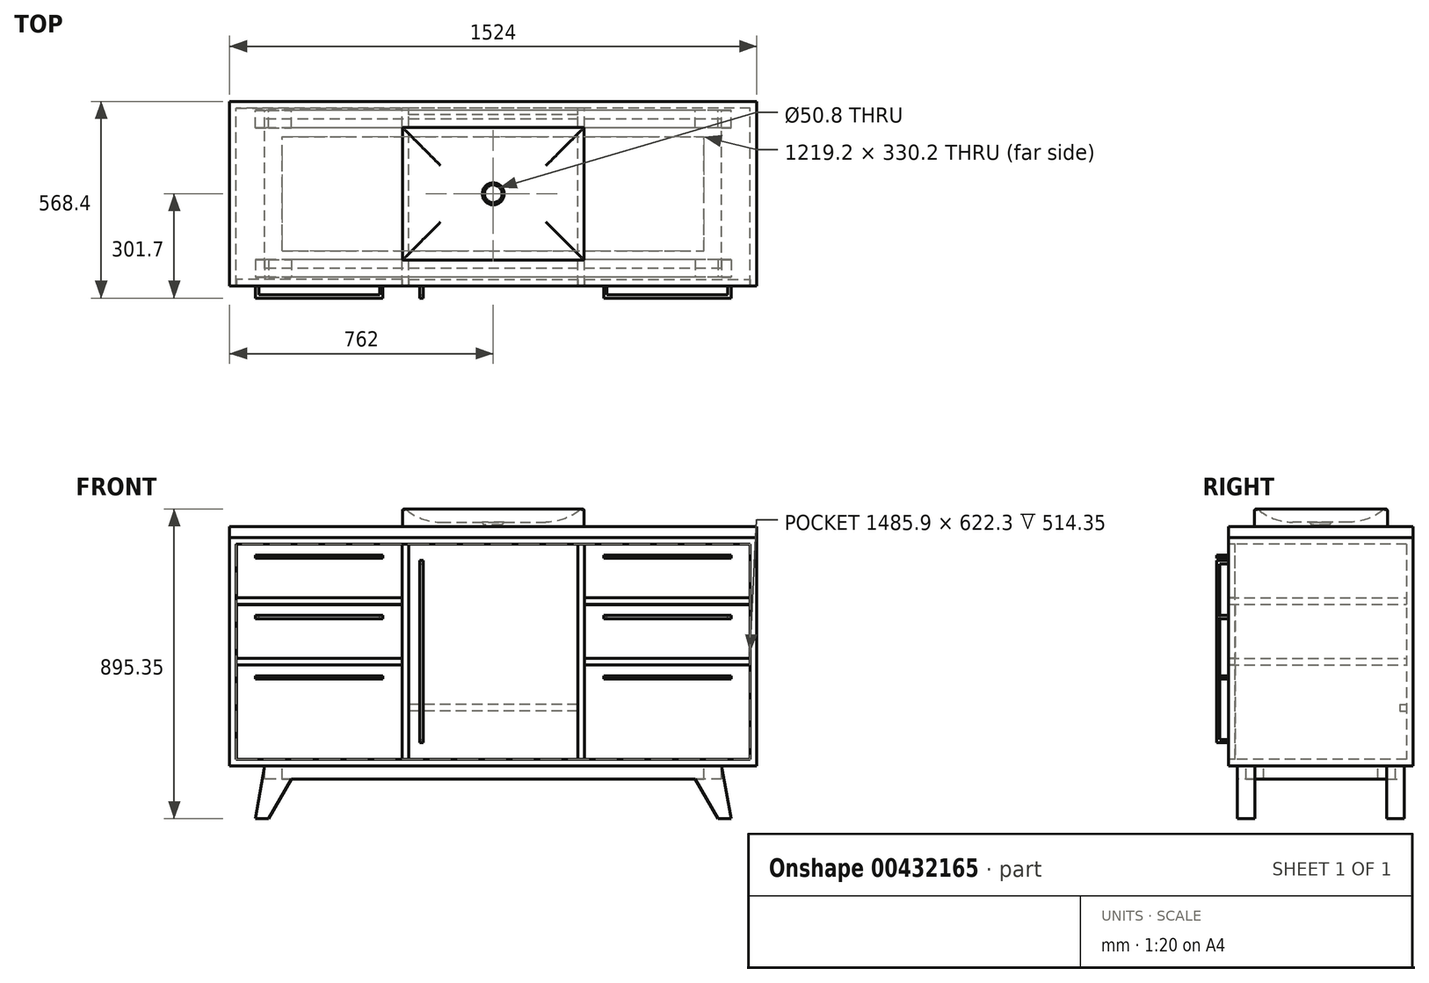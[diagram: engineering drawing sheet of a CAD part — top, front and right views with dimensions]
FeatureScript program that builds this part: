
annotation { "Feature Type Name" : "Feature", "Feature Type Description" : "" }
export const myFeature = defineFeature(function(context is Context, id is Id, definition is map)
    precondition{}
    {
        {
            var Q0;
            Q0=qCreatedBy(makeId("Front.planeOp"),FACE);
            var sketch = newSketch(context, id + "F0", { "sketchPlane" : qUnion([Q0])});
            skLineSegment(sketch, "E0.bottom", {"start": v(762, 330.2) * mm, "end": v(-762, 330.2) * mm});
            skLineSegment(sketch, "E0.top", {"start": v(762, -330.2) * mm, "end": v(-762, -330.2) * mm});
            skLineSegment(sketch, "E0.left", {"start": v(762, 330.2) * mm, "end": v(762, -330.2) * mm});
            skLineSegment(sketch, "E0.right", {"start": v(-762, 330.2) * mm, "end": v(-762, -330.2) * mm});
            skPoint(sketch, "E0.middle", {"position": v(0, 0) * mm});
            skSolve(sketch);
        }
        {
            var Q0;
            Q0=makeQuery(id+"F0.imprint","IMPRINT",FACE,{"disambiguationData":[TD([[makeQuery(id+"F0.imprint","IMPRINT",EDGE,{"derivedFrom":sQuery(id+"F0.wireOp",EDGE,"E0.bottom")}),1.0]])]});
            extrude(context, id + "F1", {"entities" : qUnion([Q0]), "oppositeDirection" : true, "depth" : 533.4 * mm});
        }
        {
            var Q0;
            Q0=makeQuery(id+"F1.opExtrude","CAP_FACE",FACE,{"disambiguationData":[OSD([sQuery(id+"F0.wireOp",EDGE,"E0.bottom"),sQuery(id+"F0.wireOp",EDGE,"E0.top"),sQuery(id+"F0.wireOp",EDGE,"E0.left"),sQuery(id+"F0.wireOp",EDGE,"E0.right")])],"isStart":true});
            var sketch = newSketch(context, id + "F2", { "sketchPlane" : qUnion([Q0])});
            skLineSegment(sketch, "E1.bottom", {"start": v(742.95, 311.15) * mm, "end": v(-742.95, 311.15) * mm});
            skLineSegment(sketch, "E1.top", {"start": v(742.95, -311.15) * mm, "end": v(-742.95, -311.15) * mm});
            skLineSegment(sketch, "E1.left", {"start": v(742.95, 311.15) * mm, "end": v(742.95, -311.15) * mm});
            skLineSegment(sketch, "E1.right", {"start": v(-742.95, 311.15) * mm, "end": v(-742.95, -311.15) * mm});
            skPoint(sketch, "E1.middle", {"position": v(0, 0) * mm});
            skSolve(sketch);
        }
        {
            var Q0;
            Q0=makeQuery(id+"F2.imprint","IMPRINT",FACE,{"disambiguationData":[TD([[makeQuery(id+"F2.imprint","IMPRINT",EDGE,{"derivedFrom":sQuery(id+"F2.wireOp",EDGE,"E1.bottom")}),1.0]])]});
            extrude(context, id + "F3", {"entities" : qUnion([Q0]), "operationType" : NewBodyOperationType.REMOVE, "oppositeDirection" : true, "depth" : 514.35 * mm});
        }
        {
            var Q0;
            Q0=makeQuery(id+"F3.boolean.opBoolean","COPY",FACE,{"derivedFrom":makeQuery(id+"F3.opExtrude","CAP_FACE",FACE,{"disambiguationData":[OSD([sQuery(id+"F2.wireOp",EDGE,"E1.bottom"),sQuery(id+"F2.wireOp",EDGE,"E1.top"),sQuery(id+"F2.wireOp",EDGE,"E1.left"),sQuery(id+"F2.wireOp",EDGE,"E1.right")])],"isStart":false})});
            var sketch = newSketch(context, id + "F4", { "sketchPlane" : qUnion([Q0])});
            skLineSegment(sketch, "E2.bottom", {"start": v(-263.52, 311.15) * mm, "end": v(-244.47, 311.15) * mm});
            skLineSegment(sketch, "E2.top", {"start": v(-263.52, -311.15) * mm, "end": v(-244.47, -311.15) * mm});
            skLineSegment(sketch, "E2.left", {"start": v(-263.53, 311.15) * mm, "end": v(-263.53, -311.15) * mm});
            skLineSegment(sketch, "E2.right", {"start": v(-244.47, 311.15) * mm, "end": v(-244.47, -311.15) * mm});
            skPoint(sketch, "E2.middle", {"position": v(-254, 0) * mm});
            skLineSegment(sketch, "E3.bottom", {"start": v(244.47, 311.15) * mm, "end": v(263.52, 311.15) * mm});
            skLineSegment(sketch, "E3.top", {"start": v(244.47, -311.15) * mm, "end": v(263.52, -311.15) * mm});
            skLineSegment(sketch, "E3.left", {"start": v(244.47, 311.15) * mm, "end": v(244.47, -311.15) * mm});
            skLineSegment(sketch, "E3.right", {"start": v(263.53, 311.15) * mm, "end": v(263.53, -311.15) * mm});
            skPoint(sketch, "E3.middle", {"position": v(254, 0) * mm});
            skLineSegment(sketch, "E4", {"start": v(-742.95, 0) * mm, "end": v(742.95, 0) * mm, "construction": true});
            skSolve(sketch);
        }
        {
            var Q0;
            Q0=makeQuery(id+"F4.imprint","IMPRINT",FACE,{"disambiguationData":[TD([[makeQuery(id+"F4.imprint","IMPRINT",EDGE,{"derivedFrom":sQuery(id+"F4.wireOp",EDGE,"E2.bottom")}),1.0]])]});
            var Q1;
            Q1=makeQuery(id+"F4.imprint","IMPRINT",FACE,{"disambiguationData":[TD([[makeQuery(id+"F4.imprint","IMPRINT",EDGE,{"derivedFrom":sQuery(id+"F4.wireOp",EDGE,"E3.bottom")}),1.0]])]});
            var Q2;
            Q2=makeQuery(id+"F1.opExtrude","CAP_FACE",FACE,{"disambiguationData":[OSD([sQuery(id+"F0.wireOp",EDGE,"E0.bottom"),sQuery(id+"F0.wireOp",EDGE,"E0.top"),sQuery(id+"F0.wireOp",EDGE,"E0.left"),sQuery(id+"F0.wireOp",EDGE,"E0.right")])],"isStart":true});
            extrude(context, id + "F5", {"entities" : qUnion([Q0, Q1]), "endBound" : BoundingType.UP_TO_SURFACE, "endBoundEntityFace" : qUnion([Q2]), "depth" : ((2 * 12) - .75 - .75) * mm});
        }
        {
            var Q0;
            Q0=makeQuery(id+"F3.boolean.opBoolean","COPY",FACE,{"derivedFrom":makeQuery(id+"F3.opExtrude","CAP_FACE",FACE,{"disambiguationData":[OSD([sQuery(id+"F2.wireOp",EDGE,"E1.bottom"),sQuery(id+"F2.wireOp",EDGE,"E1.top"),sQuery(id+"F2.wireOp",EDGE,"E1.left"),sQuery(id+"F2.wireOp",EDGE,"E1.right")])],"isStart":false})});
            var sketch = newSketch(context, id + "F6", { "sketchPlane" : qUnion([Q0])});
            skLineSegment(sketch, "E5", {"start": v(-742.95, 311.15) * mm, "end": v(-263.53, 311.15) * mm, "construction": true});
            skLineSegment(sketch, "E6.bottom", {"start": v(-742.95, 155.58) * mm, "end": v(-263.53, 155.58) * mm});
            skLineSegment(sketch, "E6.top", {"start": v(-742.95, 136.53) * mm, "end": v(-263.53, 136.53) * mm});
            skLineSegment(sketch, "E6.left", {"start": v(-742.95, 155.58) * mm, "end": v(-742.95, 136.53) * mm});
            skLineSegment(sketch, "E6.right", {"start": v(-263.53, 155.58) * mm, "end": v(-263.53, 136.53) * mm});
            skPoint(sketch, "E6.middle", {"position": v(-503.24, 146.05) * mm});
            skPoint(sketch, "E6.middle.positionSnap0", {"position": v(-503.24, 311.15) * mm});
            skPoint(sketch, "E6.centerSnap0", {"position": v(-503.24, 311.15) * mm});
            skLineSegment(sketch, "E7.bottom", {"start": v(-742.95, -19.05) * mm, "end": v(-263.53, -19.05) * mm});
            skLineSegment(sketch, "E7.top", {"start": v(-742.95, -38.1) * mm, "end": v(-263.53, -38.1) * mm});
            skLineSegment(sketch, "E7.left", {"start": v(-742.95, -19.05) * mm, "end": v(-742.95, -38.1) * mm});
            skLineSegment(sketch, "E7.right", {"start": v(-263.53, -19.05) * mm, "end": v(-263.53, -38.1) * mm});
            skPoint(sketch, "E7.middle", {"position": v(-503.24, -28.57) * mm});
            skLineSegment(sketch, "E8", {"start": v(0, 311.15) * mm, "end": v(0, -311.15) * mm, "construction": true});
            skLineSegment(sketch, "E9.MirrorCS", {"start": v(263.53, -19.05) * mm, "end": v(263.53, -38.1) * mm});
            skLineSegment(sketch, "E10.MirrorCS", {"start": v(742.95, -19.05) * mm, "end": v(742.95, -38.1) * mm});
            skLineSegment(sketch, "E11.MirrorCS", {"start": v(742.95, 155.58) * mm, "end": v(742.95, 136.53) * mm});
            skLineSegment(sketch, "E12.MirrorCS", {"start": v(263.53, 155.58) * mm, "end": v(263.53, 136.53) * mm});
            skPoint(sketch, "E13.MirrorP", {"position": v(503.24, 311.15) * mm});
            skLineSegment(sketch, "E14.MirrorCS", {"start": v(742.95, 155.58) * mm, "end": v(263.53, 155.57) * mm});
            skPoint(sketch, "E15.MirrorP", {"position": v(503.24, -28.57) * mm});
            skLineSegment(sketch, "E16.MirrorCS", {"start": v(742.95, -38.1) * mm, "end": v(263.53, -38.1) * mm});
            skLineSegment(sketch, "E17.MirrorCS", {"start": v(742.95, -19.05) * mm, "end": v(263.53, -19.05) * mm});
            skLineSegment(sketch, "E18.MirrorCS", {"start": v(742.95, 136.53) * mm, "end": v(263.53, 136.53) * mm});
            skLineSegment(sketch, "E19.MirrorCS", {"start": v(742.95, 311.15) * mm, "end": v(263.53, 311.15) * mm, "construction": true});
            skPoint(sketch, "E20.MirrorP", {"position": v(503.24, 146.05) * mm});
            skPoint(sketch, "E21.cornerSnap0", {"position": v(-503.24, -19.05) * mm});
            skPoint(sketch, "E22.middle", {"position": v(0, 146.05) * mm});
            skLineSegment(sketch, "E23.bottom", {"start": v(244.47, -152.4) * mm, "end": v(-244.47, -152.4) * mm});
            skLineSegment(sketch, "E23.top", {"start": v(244.47, -171.45) * mm, "end": v(-244.47, -171.45) * mm});
            skLineSegment(sketch, "E23.left", {"start": v(244.47, -152.4) * mm, "end": v(244.47, -171.45) * mm});
            skLineSegment(sketch, "E23.right", {"start": v(-244.47, -152.4) * mm, "end": v(-244.47, -171.45) * mm});
            skPoint(sketch, "E23.middle", {"position": v(0, -161.93) * mm});
            skSolve(sketch);
        }
        {
            var Q0;
            Q0=makeQuery(id+"F6.imprint","IMPRINT",FACE,{"disambiguationData":[TD([[makeQuery(id+"F6.imprint","IMPRINT",EDGE,{"derivedFrom":sQuery(id+"F6.wireOp",EDGE,"E6.bottom")}),-1.0]])]});
            var Q1;
            Q1=makeQuery(id+"F6.imprint","IMPRINT",FACE,{"disambiguationData":[TD([[makeQuery(id+"F6.imprint","IMPRINT",EDGE,{"derivedFrom":sQuery(id+"F6.wireOp",EDGE,"E7.bottom")}),-1.0]])]});
            var Q2;
            Q2=makeQuery(id+"F6.imprint","IMPRINT",FACE,{"disambiguationData":[TD([[makeQuery(id+"F6.imprint","IMPRINT",EDGE,{"derivedFrom":sQuery(id+"F6.wireOp",EDGE,"E11.MirrorCS")}),-1.0]])]});
            var Q3;
            Q3=makeQuery(id+"F6.imprint","IMPRINT",FACE,{"disambiguationData":[TD([[makeQuery(id+"F6.imprint","IMPRINT",EDGE,{"derivedFrom":sQuery(id+"F6.wireOp",EDGE,"E9.MirrorCS")}),1.0]])]});
            var Q4;
            Q4=makeQuery(id+"F1.opExtrude","CAP_FACE",FACE,{"disambiguationData":[OSD([sQuery(id+"F0.wireOp",EDGE,"E0.bottom"),sQuery(id+"F0.wireOp",EDGE,"E0.top"),sQuery(id+"F0.wireOp",EDGE,"E0.left"),sQuery(id+"F0.wireOp",EDGE,"E0.right")])],"isStart":true});
            extrude(context, id + "F7", {"entities" : qUnion([Q0, Q1, Q2, Q3]), "endBound" : BoundingType.UP_TO_SURFACE, "endBoundEntityFace" : qUnion([Q4]), "depth" : 571.5 * mm});
        }
        {
            var Q0;
            Q0=makeQuery(id+"F7.opExtrude","CAP_FACE",FACE,{"disambiguationData":[OSD([sQuery(id+"F6.wireOp",EDGE,"E7.bottom"),sQuery(id+"F6.wireOp",EDGE,"E7.top"),sQuery(id+"F6.wireOp",EDGE,"E7.left"),sQuery(id+"F6.wireOp",EDGE,"E7.right")])],"isStart":false});
            var sketch = newSketch(context, id + "F8", { "sketchPlane" : qUnion([Q0])});
            skLineSegment(sketch, "E24.bottom", {"start": v(-742.95, -38.1) * mm, "end": v(-263.53, -38.1) * mm, "construction": true});
            skLineSegment(sketch, "E24.top", {"start": v(-742.95, -311.15) * mm, "end": v(-263.53, -311.15) * mm, "construction": true});
            skLineSegment(sketch, "E24.left", {"start": v(-742.95, -38.1) * mm, "end": v(-742.95, -311.15) * mm, "construction": true});
            skLineSegment(sketch, "E24.right", {"start": v(-263.52, -38.1) * mm, "end": v(-263.52, -311.15) * mm, "construction": true});
            skLineSegment(sketch, "E25.bottom", {"start": v(-742.95, -19.05) * mm, "end": v(-263.53, -19.05) * mm, "construction": true});
            skLineSegment(sketch, "E25.top", {"start": v(-742.95, 136.53) * mm, "end": v(-263.53, 136.53) * mm, "construction": true});
            skLineSegment(sketch, "E25.left", {"start": v(-742.95, -19.05) * mm, "end": v(-742.95, 136.53) * mm, "construction": true});
            skLineSegment(sketch, "E25.right", {"start": v(-263.53, -19.05) * mm, "end": v(-263.53, 136.53) * mm, "construction": true});
            skLineSegment(sketch, "E26.bottom", {"start": v(-742.95, 311.15) * mm, "end": v(-263.53, 311.15) * mm, "construction": true});
            skLineSegment(sketch, "E26.top", {"start": v(-742.95, 155.58) * mm, "end": v(-263.53, 155.58) * mm, "construction": true});
            skLineSegment(sketch, "E26.left", {"start": v(-742.95, 311.15) * mm, "end": v(-742.95, 155.58) * mm, "construction": true});
            skLineSegment(sketch, "E26.right", {"start": v(-263.52, 311.15) * mm, "end": v(-263.52, 155.58) * mm, "construction": true});
            skLineSegment(sketch, "E27", {"start": v(0, 311.15) * mm, "end": v(0, -311.15) * mm, "construction": true});
            skLineSegment(sketch, "E28.bottom", {"start": v(-263.92, 155.97) * mm, "end": v(-742.55, 155.97) * mm});
            skLineSegment(sketch, "E28.top", {"start": v(-263.92, 310.75) * mm, "end": v(-742.55, 310.75) * mm});
            skLineSegment(sketch, "E28.left", {"start": v(-263.92, 155.97) * mm, "end": v(-263.92, 310.75) * mm});
            skLineSegment(sketch, "E28.right", {"start": v(-742.55, 155.97) * mm, "end": v(-742.55, 310.75) * mm});
            skPoint(sketch, "E28.middle", {"position": v(-503.24, 233.36) * mm});
            skPoint(sketch, "E28.middle.positionSnap0", {"position": v(-503.24, 311.15) * mm});
            skPoint(sketch, "E28.middle.positionSnap1", {"position": v(-742.95, 233.36) * mm});
            skPoint(sketch, "E28.centerSnap0", {"position": v(-503.24, 311.15) * mm});
            skPoint(sketch, "E28.centerSnap1", {"position": v(-742.95, 233.36) * mm});
            skPoint(sketch, "E29.middle.positionSnap0", {"position": v(-503.24, 136.53) * mm});
            skPoint(sketch, "E29.middle.positionSnap1", {"position": v(-742.95, 58.74) * mm});
            skPoint(sketch, "E29.centerSnap0", {"position": v(-503.24, 136.53) * mm});
            skPoint(sketch, "E29.centerSnap1", {"position": v(-742.95, 58.74) * mm});
            skLineSegment(sketch, "E30.bottom", {"start": v(-263.92, -38.5) * mm, "end": v(-742.55, -38.5) * mm});
            skLineSegment(sketch, "E30.top", {"start": v(-263.92, -310.75) * mm, "end": v(-742.55, -310.75) * mm});
            skLineSegment(sketch, "E30.left", {"start": v(-263.92, -38.5) * mm, "end": v(-263.92, -310.75) * mm});
            skLineSegment(sketch, "E30.right", {"start": v(-742.55, -38.5) * mm, "end": v(-742.55, -310.75) * mm});
            skPoint(sketch, "E30.middle", {"position": v(-503.24, -174.63) * mm});
            skPoint(sketch, "E30.middle.positionSnap0", {"position": v(-742.95, -174.63) * mm});
            skPoint(sketch, "E30.middle.positionSnap1", {"position": v(-503.24, -38.1) * mm});
            skPoint(sketch, "E30.centerSnap0", {"position": v(-742.95, -174.63) * mm});
            skPoint(sketch, "E30.centerSnap1", {"position": v(-503.24, -38.1) * mm});
            skLineSegment(sketch, "E31.bottom", {"start": v(-742.55, 136.13) * mm, "end": v(-263.92, 136.13) * mm});
            skLineSegment(sketch, "E31.top", {"start": v(-742.55, -18.65) * mm, "end": v(-263.92, -18.65) * mm});
            skLineSegment(sketch, "E31.left", {"start": v(-742.55, 136.13) * mm, "end": v(-742.55, -18.65) * mm});
            skLineSegment(sketch, "E31.right", {"start": v(-263.92, 136.13) * mm, "end": v(-263.92, -18.65) * mm});
            skPoint(sketch, "E31.middle", {"position": v(-503.24, 58.74) * mm});
            skLineSegment(sketch, "E32.MirrorCS", {"start": v(742.55, 155.97) * mm, "end": v(742.55, 310.75) * mm});
            skLineSegment(sketch, "E33.MirrorCS", {"start": v(742.55, 136.13) * mm, "end": v(742.55, -18.65) * mm});
            skLineSegment(sketch, "E34.MirrorCS", {"start": v(263.92, -310.75) * mm, "end": v(742.55, -310.75) * mm});
            skPoint(sketch, "E35.MirrorP", {"position": v(742.95, -174.62) * mm});
            skLineSegment(sketch, "E36.MirrorCS", {"start": v(742.55, -18.65) * mm, "end": v(263.92, -18.65) * mm});
            skLineSegment(sketch, "E37.MirrorCS", {"start": v(263.92, 155.97) * mm, "end": v(742.55, 155.97) * mm});
            skLineSegment(sketch, "E38.MirrorCS", {"start": v(263.92, -38.5) * mm, "end": v(263.92, -310.75) * mm});
            skPoint(sketch, "E39.MirrorP", {"position": v(503.24, 311.15) * mm});
            skPoint(sketch, "E40.MirrorP", {"position": v(503.24, -38.1) * mm});
            skLineSegment(sketch, "E41.MirrorCS", {"start": v(263.92, 310.75) * mm, "end": v(742.55, 310.75) * mm});
            skLineSegment(sketch, "E42.MirrorCS", {"start": v(742.55, 136.13) * mm, "end": v(263.92, 136.13) * mm});
            skPoint(sketch, "E43.MirrorP", {"position": v(742.95, 233.36) * mm});
            skLineSegment(sketch, "E44.MirrorCS", {"start": v(263.92, 155.97) * mm, "end": v(263.92, 310.75) * mm});
            skLineSegment(sketch, "E45.MirrorCS", {"start": v(742.55, -38.5) * mm, "end": v(742.55, -310.75) * mm});
            skPoint(sketch, "E46.MirrorP", {"position": v(503.24, 136.53) * mm});
            skLineSegment(sketch, "E47.MirrorCS", {"start": v(263.92, 136.13) * mm, "end": v(263.92, -18.65) * mm});
            skPoint(sketch, "E48.MirrorP", {"position": v(742.95, 58.74) * mm});
            skPoint(sketch, "E49.MirrorP", {"position": v(503.24, 233.36) * mm});
            skLineSegment(sketch, "E50.MirrorCS", {"start": v(742.95, -311.15) * mm, "end": v(263.53, -311.15) * mm, "construction": true});
            skLineSegment(sketch, "E51.MirrorCS", {"start": v(742.95, -19.05) * mm, "end": v(742.95, 136.53) * mm, "construction": true});
            skLineSegment(sketch, "E52.MirrorCS", {"start": v(742.95, -38.1) * mm, "end": v(742.95, -311.15) * mm, "construction": true});
            skPoint(sketch, "E53.MirrorP", {"position": v(503.24, 58.74) * mm});
            skLineSegment(sketch, "E54.MirrorCS", {"start": v(263.52, -38.1) * mm, "end": v(263.52, -311.15) * mm, "construction": true});
            skLineSegment(sketch, "E55.MirrorCS", {"start": v(742.95, -19.05) * mm, "end": v(263.53, -19.05) * mm, "construction": true});
            skLineSegment(sketch, "E56.MirrorCS", {"start": v(263.52, 311.15) * mm, "end": v(263.52, 155.58) * mm, "construction": true});
            skLineSegment(sketch, "E57.MirrorCS", {"start": v(742.95, 311.15) * mm, "end": v(742.95, 155.58) * mm, "construction": true});
            skLineSegment(sketch, "E58.MirrorCS", {"start": v(742.95, -38.1) * mm, "end": v(263.53, -38.1) * mm, "construction": true});
            skLineSegment(sketch, "E59.MirrorCS", {"start": v(742.95, 155.58) * mm, "end": v(263.53, 155.58) * mm, "construction": true});
            skLineSegment(sketch, "E60.MirrorCS", {"start": v(742.95, 136.53) * mm, "end": v(263.53, 136.53) * mm, "construction": true});
            skPoint(sketch, "E61.MirrorP", {"position": v(503.24, -174.62) * mm});
            skLineSegment(sketch, "E62.MirrorCS", {"start": v(263.53, -19.05) * mm, "end": v(263.53, 136.53) * mm, "construction": true});
            skLineSegment(sketch, "E63.MirrorCS", {"start": v(263.92, -38.5) * mm, "end": v(742.55, -38.5) * mm});
            skLineSegment(sketch, "E64.MirrorCS", {"start": v(742.95, 311.15) * mm, "end": v(263.53, 311.15) * mm, "construction": true});
            skSolve(sketch);
        }
        {
            var Q0;
            Q0=makeQuery(id+"F8.imprint","IMPRINT",FACE,{"disambiguationData":[TD([[makeQuery(id+"F8.imprint","IMPRINT",EDGE,{"derivedFrom":sQuery(id+"F8.wireOp",EDGE,"E28.bottom")}),-1.0]])]});
            var Q1;
            Q1=makeQuery(id+"F8.imprint","IMPRINT",FACE,{"disambiguationData":[TD([[makeQuery(id+"F8.imprint","IMPRINT",EDGE,{"derivedFrom":sQuery(id+"F8.wireOp",EDGE,"E31.bottom")}),-1.0]])]});
            var Q2;
            Q2=makeQuery(id+"F8.imprint","IMPRINT",FACE,{"disambiguationData":[TD([[makeQuery(id+"F8.imprint","IMPRINT",EDGE,{"derivedFrom":sQuery(id+"F8.wireOp",EDGE,"E30.bottom")}),1.0]])]});
            var Q3;
            Q3=makeQuery(id+"F8.imprint","IMPRINT",FACE,{"disambiguationData":[TD([[makeQuery(id+"F8.imprint","IMPRINT",EDGE,{"derivedFrom":sQuery(id+"F8.wireOp",EDGE,"E32.MirrorCS")}),1.0]])]});
            var Q4;
            Q4=makeQuery(id+"F8.imprint","IMPRINT",FACE,{"disambiguationData":[TD([[makeQuery(id+"F8.imprint","IMPRINT",EDGE,{"derivedFrom":sQuery(id+"F8.wireOp",EDGE,"E33.MirrorCS")}),-1.0]])]});
            var Q5;
            Q5=makeQuery(id+"F8.imprint","IMPRINT",FACE,{"disambiguationData":[TD([[makeQuery(id+"F8.imprint","IMPRINT",EDGE,{"derivedFrom":sQuery(id+"F8.wireOp",EDGE,"E34.MirrorCS")}),1.0]])]});
            extrude(context, id + "F9", {"entities" : qUnion([Q0, Q1, Q2, Q3, Q4, Q5]), "oppositeDirection" : true, "depth" : 19.05 * mm});
        }
        {
            var Q0;
            Q0=qCreatedBy(makeId("Front.planeOp"),FACE);
            var sketch = newSketch(context, id + "F10", { "sketchPlane" : qUnion([Q0])});
            skLineSegment(sketch, "E65.bottom", {"start": v(-244.08, -310.75) * mm, "end": v(244.08, -310.75) * mm});
            skLineSegment(sketch, "E65.top", {"start": v(-244.08, 310.75) * mm, "end": v(244.08, 310.75) * mm});
            skLineSegment(sketch, "E65.left", {"start": v(-244.08, -310.75) * mm, "end": v(-244.08, 310.75) * mm});
            skLineSegment(sketch, "E65.right", {"start": v(244.08, -310.75) * mm, "end": v(244.08, 310.75) * mm});
            skPoint(sketch, "E65.middle", {"position": v(0, 0) * mm});
            skSolve(sketch);
        }
        {
            var Q0;
            Q0=makeQuery(id+"F10.imprint","IMPRINT",FACE,{"disambiguationData":[TD([[makeQuery(id+"F10.imprint","IMPRINT",EDGE,{"derivedFrom":sQuery(id+"F10.wireOp",EDGE,"E65.bottom")}),1.0]])]});
            extrude(context, id + "F11", {"entities" : qUnion([Q0]), "oppositeDirection" : true, "depth" : 19.05 * mm});
        }
        {
            var Q0;
            Q0=makeQuery(id+"F6.imprint","IMPRINT",FACE,{"disambiguationData":[TD([[makeQuery(id+"F6.imprint","IMPRINT",EDGE,{"derivedFrom":sQuery(id+"F6.wireOp",EDGE,"E23.bottom")}),1.0]])]});
            extrude(context, id + "F12", {"entities" : qUnion([Q0]), "depth" : ((21 - .75 - .75) - .3125) * mm});
        }
        {
            var Q0;
            Q0=makeQuery(id+"F1.opExtrude","SWEPT_FACE",FACE,{"disambiguationData":[OSD([sQuery(id+"F0.wireOp",EDGE,"E0.top")])]});
            var sketch = newSketch(context, id + "F13", { "sketchPlane" : qUnion([Q0])});
            skLineSegment(sketch, "E66.bottom", {"start": v(660.4, -50.8) * mm, "end": v(-660.4, -50.8) * mm});
            skLineSegment(sketch, "E66.top", {"start": v(660.4, -482.6) * mm, "end": v(-660.4, -482.6) * mm});
            skLineSegment(sketch, "E66.left", {"start": v(660.4, -50.8) * mm, "end": v(660.4, -482.6) * mm});
            skLineSegment(sketch, "E66.right", {"start": v(-660.4, -50.8) * mm, "end": v(-660.4, -482.6) * mm});
            skPoint(sketch, "E66.middle", {"position": v(0, -266.7) * mm});
            skPoint(sketch, "E66.middle.positionSnap0", {"position": v(-762, -266.7) * mm});
            skPoint(sketch, "E66.centerSnap0", {"position": v(-762, -266.7) * mm});
            skLineSegment(sketch, "E67.bottom", {"start": v(-609.6, -101.6) * mm, "end": v(609.6, -101.6) * mm});
            skLineSegment(sketch, "E67.top", {"start": v(-609.6, -431.8) * mm, "end": v(609.6, -431.8) * mm});
            skLineSegment(sketch, "E67.left", {"start": v(-609.6, -101.6) * mm, "end": v(-609.6, -431.8) * mm});
            skLineSegment(sketch, "E67.right", {"start": v(609.6, -101.6) * mm, "end": v(609.6, -431.8) * mm});
            skSolve(sketch);
        }
        {
            var Q0;
            Q0=makeQuery(id+"F13.imprint","IMPRINT",FACE,{"disambiguationData":[TD([[makeQuery(id+"F13.imprint","IMPRINT",EDGE,{"derivedFrom":sQuery(id+"F13.wireOp",EDGE,"E66.bottom")}),1.0]])]});
            extrude(context, id + "F14", {"entities" : qUnion([Q0]), "depth" : 38.1 * mm});
        }
        {
            var Q0;
            Q0=makeQuery(id+"F14.opExtrude","SWEPT_FACE",FACE,{"disambiguationData":[OSD([sQuery(id+"F13.wireOp",EDGE,"E66.bottom")])]});
            var sketch = newSketch(context, id + "F15", { "sketchPlane" : qUnion([Q0])});
            skLineSegment(sketch, "E68", {"start": v(-660.4, -330.2) * mm, "end": v(-687.27, -482.6) * mm});
            skLineSegment(sketch, "E69", {"start": v(-687.27, -482.6) * mm, "end": v(-649.17, -482.6) * mm});
            skLineSegment(sketch, "E70", {"start": v(-649.17, -482.6) * mm, "end": v(-583.18, -368.3) * mm});
            skLineSegment(sketch, "E71", {"start": v(0, -330.2) * mm, "end": v(0, -368.3) * mm, "construction": true});
            skLineSegment(sketch, "E72.MirrorCS", {"start": v(687.27, -482.6) * mm, "end": v(649.17, -482.6) * mm});
            skLineSegment(sketch, "E73.MirrorCS", {"start": v(660.4, -330.2) * mm, "end": v(687.27, -482.6) * mm});
            skLineSegment(sketch, "E74.MirrorCS", {"start": v(649.17, -482.6) * mm, "end": v(583.18, -368.3) * mm});
            skLineSegment(sketch, "E75", {"start": v(-583.18, -368.3) * mm, "end": v(583.18, -368.3) * mm});
            skLineSegment(sketch, "E76", {"start": v(-660.4, -330.2) * mm, "end": v(660.4, -330.2) * mm});
            skSolve(sketch);
        }
        {
            var Q0;
            Q0=makeQuery(id+"F10.imprint","IMPRINT",FACE,{"disambiguationData":[TD([[makeQuery(id+"F10.imprint","IMPRINT",EDGE,{"derivedFrom":sQuery(id+"F10.wireOp",EDGE,"E65.bottom")}),1.0]])]});
            cPlane(context, id + "F16", {"entities" : qUnion([Q0]), "cplaneType" : CPlaneType.OFFSET, "offset" : 266.7 * mm, "oppositeDirection" : true, "width" : 152.4 * mm, "height" : 152.4 * mm});
        }
        {
            var Q0;
            Q0 = qSketchRegion(id + "F15", true);
            extrude(context, id + "F17", {"entities" : qUnion([Q0]), "oppositeDirection" : true, "depth" : 25.4 * mm, "hasSecondDirection" : true, "secondDirectionOppositeDirection" : false, "secondDirectionDepth" : 25.4 * mm});
        }
        {
            var Q0;
            Q0=makeQuery(id+"F17.opExtrude","SWEPT_BODY",BODY,{"disambiguationData":[OSD([sQuery(id+"F15.wireOp",EDGE,"E68"),sQuery(id+"F15.wireOp",EDGE,"E69"),sQuery(id+"F15.wireOp",EDGE,"E70"),sQuery(id+"F15.wireOp",EDGE,"E72.MirrorCS"),sQuery(id+"F15.wireOp",EDGE,"E73.MirrorCS"),sQuery(id+"F15.wireOp",EDGE,"E74.MirrorCS"),sQuery(id+"F15.wireOp",EDGE,"E75"),sQuery(id+"F15.wireOp",EDGE,"E76")])]});
            var Q1;
            Q1=qCreatedBy(id+"F16.planeOp",FACE);
            mirror(context, id + "F18", {"entities" : qUnion([Q0]), "mirrorPlane" : qUnion([Q1])});
        }
        {
            var Q0;
            Q0=makeQuery(id+"F1.opExtrude","SWEPT_FACE",FACE,{"disambiguationData":[OSD([sQuery(id+"F0.wireOp",EDGE,"E0.bottom")])]});
            var sketch = newSketch(context, id + "F19", { "sketchPlane" : qUnion([Q0])});
            skLineSegment(sketch, "E77.bottom", {"start": v(-762, 533.4) * mm, "end": v(762, 533.4) * mm});
            skLineSegment(sketch, "E77.top", {"start": v(-762, 0) * mm, "end": v(762, 0) * mm});
            skLineSegment(sketch, "E77.left", {"start": v(-762, 533.4) * mm, "end": v(-762, 0) * mm});
            skLineSegment(sketch, "E77.right", {"start": v(762, 533.4) * mm, "end": v(762, 0) * mm});
            skPoint(sketch, "E77.middle", {"position": v(0, 266.7) * mm});
            skPoint(sketch, "E77.middle.positionSnap0", {"position": v(0, 533.4) * mm});
            skPoint(sketch, "E77.middle.positionSnap1", {"position": v(-762, 266.7) * mm});
            skPoint(sketch, "E77.centerSnap0", {"position": v(0, 533.4) * mm});
            skPoint(sketch, "E77.centerSnap1", {"position": v(-762, 266.7) * mm});
            skSolve(sketch);
        }
        {
            var Q0;
            Q0=makeQuery(id+"F19.imprint","IMPRINT",FACE,{"disambiguationData":[TD([[makeQuery(id+"F19.imprint","IMPRINT",EDGE,{"derivedFrom":sQuery(id+"F19.wireOp",EDGE,"E77.bottom")}),1.0]])]});
            extrude(context, id + "F20", {"entities" : qUnion([Q0]), "depth" : 31.75 * mm});
        }
        {
            var Q0;
            Q0=makeQuery(id+"F11.opExtrude","CAP_FACE",FACE,{"disambiguationData":[OSD([sQuery(id+"F10.wireOp",EDGE,"E65.bottom"),sQuery(id+"F10.wireOp",EDGE,"E65.top"),sQuery(id+"F10.wireOp",EDGE,"E65.left"),sQuery(id+"F10.wireOp",EDGE,"E65.right")])],"isStart":true});
            var sketch = newSketch(context, id + "F21", { "sketchPlane" : qUnion([Q0])});
            skLineSegment(sketch, "E78.bottom", {"start": v(-212.33, 263.5) * mm, "end": v(-202.8, 263.5) * mm});
            skLineSegment(sketch, "E78.top", {"start": v(-212.33, -263.5) * mm, "end": v(-202.8, -263.5) * mm});
            skLineSegment(sketch, "E78.left", {"start": v(-212.33, 263.5) * mm, "end": v(-212.33, -263.5) * mm});
            skLineSegment(sketch, "E78.right", {"start": v(-202.8, 263.5) * mm, "end": v(-202.8, -263.5) * mm});
            skLineSegment(sketch, "E79", {"start": v(-202.8, 0) * mm, "end": v(0, 0) * mm, "construction": true});
            skSolve(sketch);
        }
        {
            var Q0;
            Q0=makeQuery(id+"F21.imprint","IMPRINT",FACE,{"disambiguationData":[TD([[makeQuery(id+"F21.imprint","IMPRINT",EDGE,{"derivedFrom":sQuery(id+"F21.wireOp",EDGE,"E78.bottom")}),-1.0]])]});
            extrude(context, id + "F22", {"entities" : qUnion([Q0]), "depth" : 35 * mm});
        }
        {
            var Q0;
            Q0=makeQuery(id+"F22.opExtrude","SWEPT_FACE",FACE,{"disambiguationData":[OSD([sQuery(id+"F21.wireOp",EDGE,"E78.right")])]});
            var sketch = newSketch(context, id + "F23", { "sketchPlane" : qUnion([Q0])});
            skLineSegment(sketch, "E80.bottom", {"start": v(0, 253.97) * mm, "end": v(-25.48, 253.97) * mm});
            skLineSegment(sketch, "E80.top", {"start": v(0, -253.98) * mm, "end": v(-25.48, -253.98) * mm});
            skLineSegment(sketch, "E80.left", {"start": v(0, 253.97) * mm, "end": v(0, -253.98) * mm});
            skLineSegment(sketch, "E80.right", {"start": v(-25.48, 253.97) * mm, "end": v(-25.48, -253.98) * mm});
            skSolve(sketch);
        }
        {
            var Q0;
            Q0=makeQuery(id+"F23.imprint","IMPRINT",FACE,{"disambiguationData":[TD([[makeQuery(id+"F23.imprint","IMPRINT",EDGE,{"derivedFrom":sQuery(id+"F23.wireOp",EDGE,"E80.bottom")}),1.0]])]});
            extrude(context, id + "F24", {"entities" : qUnion([Q0]), "operationType" : NewBodyOperationType.REMOVE, "oppositeDirection" : true, "depth" : 25.4 * mm});
        }
        {
            var Q0;
            Q0=makeQuery(id+"F9.opExtrude","CAP_FACE",FACE,{"disambiguationData":[OSD([sQuery(id+"F8.wireOp",EDGE,"E32.MirrorCS"),sQuery(id+"F8.wireOp",EDGE,"E37.MirrorCS"),sQuery(id+"F8.wireOp",EDGE,"E41.MirrorCS"),sQuery(id+"F8.wireOp",EDGE,"E44.MirrorCS")])],"isStart":true});
            var sketch = newSketch(context, id + "F25", { "sketchPlane" : qUnion([Q0])});
            skLineSegment(sketch, "E81.bottom", {"start": v(687.24, 269.88) * mm, "end": v(319.24, 269.88) * mm});
            skLineSegment(sketch, "E81.top", {"start": v(687.24, 279.4) * mm, "end": v(319.24, 279.4) * mm});
            skLineSegment(sketch, "E81.left", {"start": v(687.24, 269.88) * mm, "end": v(687.24, 279.4) * mm});
            skLineSegment(sketch, "E81.right", {"start": v(319.24, 269.88) * mm, "end": v(319.24, 279.4) * mm});
            skPoint(sketch, "E81.middle", {"position": v(503.24, 274.64) * mm});
            skPoint(sketch, "E81.middle.positionSnap0", {"position": v(503.24, 310.75) * mm});
            skPoint(sketch, "E81.centerSnap0", {"position": v(503.24, 310.75) * mm});
            skLineSegment(sketch, "E82.bottom", {"start": v(687.24, 104.78) * mm, "end": v(319.24, 104.78) * mm});
            skLineSegment(sketch, "E82.top", {"start": v(687.24, 95.25) * mm, "end": v(319.24, 95.25) * mm});
            skLineSegment(sketch, "E82.left", {"start": v(687.24, 104.78) * mm, "end": v(687.24, 95.25) * mm});
            skLineSegment(sketch, "E82.right", {"start": v(319.24, 104.78) * mm, "end": v(319.24, 95.25) * mm});
            skPoint(sketch, "E82.middle", {"position": v(503.24, 100.01) * mm});
            skLineSegment(sketch, "E83.bottom", {"start": v(687.24, -69.85) * mm, "end": v(319.24, -69.85) * mm});
            skLineSegment(sketch, "E83.top", {"start": v(687.24, -79.37) * mm, "end": v(319.24, -79.37) * mm});
            skLineSegment(sketch, "E83.left", {"start": v(687.24, -69.85) * mm, "end": v(687.24, -79.37) * mm});
            skLineSegment(sketch, "E83.right", {"start": v(319.24, -69.85) * mm, "end": v(319.24, -79.37) * mm});
            skPoint(sketch, "E83.middle", {"position": v(503.24, -74.61) * mm});
            skPoint(sketch, "E83.middle.positionSnap0", {"position": v(503.24, 95.25) * mm});
            skPoint(sketch, "E83.centerSnap0", {"position": v(503.24, 95.25) * mm});
            skLineSegment(sketch, "E84", {"start": v(0, 310.75) * mm, "end": v(0, -311.15) * mm, "construction": true});
            skLineSegment(sketch, "E85.MirrorCS", {"start": v(-687.24, 104.78) * mm, "end": v(-687.24, 95.25) * mm});
            skLineSegment(sketch, "E86.MirrorCS", {"start": v(-319.24, 104.78) * mm, "end": v(-319.24, 95.25) * mm});
            skLineSegment(sketch, "E87.MirrorCS", {"start": v(-319.24, -69.85) * mm, "end": v(-319.24, -79.37) * mm});
            skLineSegment(sketch, "E88.MirrorCS", {"start": v(-687.24, -69.85) * mm, "end": v(-687.24, -79.37) * mm});
            skLineSegment(sketch, "E89.MirrorCS", {"start": v(-687.24, 269.88) * mm, "end": v(-687.24, 279.4) * mm});
            skLineSegment(sketch, "E90.MirrorCS", {"start": v(-319.24, 269.88) * mm, "end": v(-319.24, 279.4) * mm});
            skPoint(sketch, "E91.MirrorP", {"position": v(-503.24, 95.25) * mm});
            skPoint(sketch, "E92.MirrorP", {"position": v(-503.24, 310.75) * mm});
            skPoint(sketch, "E93.MirrorP", {"position": v(-503.24, 100.01) * mm});
            skLineSegment(sketch, "E94.MirrorCS", {"start": v(-687.24, 269.88) * mm, "end": v(-319.24, 269.88) * mm});
            skLineSegment(sketch, "E95.MirrorCS", {"start": v(-687.24, 279.4) * mm, "end": v(-319.24, 279.4) * mm});
            skLineSegment(sketch, "E96.MirrorCS", {"start": v(-687.24, -69.85) * mm, "end": v(-319.24, -69.85) * mm});
            skLineSegment(sketch, "E97.MirrorCS", {"start": v(-687.24, -79.37) * mm, "end": v(-319.24, -79.37) * mm});
            skLineSegment(sketch, "E98.MirrorCS", {"start": v(-687.24, 95.25) * mm, "end": v(-319.24, 95.25) * mm});
            skPoint(sketch, "E99.MirrorP", {"position": v(-503.24, 274.64) * mm});
            skLineSegment(sketch, "E100.MirrorCS", {"start": v(-687.24, 104.78) * mm, "end": v(-319.24, 104.78) * mm});
            skPoint(sketch, "E101.MirrorP", {"position": v(-503.24, -74.61) * mm});
            skSolve(sketch);
        }
        {
            var Q0;
            Q0=makeQuery(id+"F25.imprint","IMPRINT",FACE,{"disambiguationData":[TD([[makeQuery(id+"F25.imprint","IMPRINT",EDGE,{"derivedFrom":sQuery(id+"F25.wireOp",EDGE,"E89.MirrorCS")}),-1.0]])]});
            var Q1;
            Q1=makeQuery(id+"F25.imprint","IMPRINT",FACE,{"disambiguationData":[TD([[makeQuery(id+"F25.imprint","IMPRINT",EDGE,{"derivedFrom":sQuery(id+"F25.wireOp",EDGE,"E85.MirrorCS")}),1.0]])]});
            var Q2;
            Q2=makeQuery(id+"F25.imprint","IMPRINT",FACE,{"disambiguationData":[TD([[makeQuery(id+"F25.imprint","IMPRINT",EDGE,{"derivedFrom":sQuery(id+"F25.wireOp",EDGE,"E87.MirrorCS")}),-1.0]])]});
            var Q3;
            Q3=makeQuery(id+"F25.imprint","IMPRINT",FACE,{"disambiguationData":[TD([[makeQuery(id+"F25.imprint","IMPRINT",EDGE,{"derivedFrom":sQuery(id+"F25.wireOp",EDGE,"E81.bottom")}),-1.0]])]});
            var Q4;
            Q4=makeQuery(id+"F25.imprint","IMPRINT",FACE,{"disambiguationData":[TD([[makeQuery(id+"F25.imprint","IMPRINT",EDGE,{"derivedFrom":sQuery(id+"F25.wireOp",EDGE,"E82.bottom")}),1.0]])]});
            var Q5;
            Q5=makeQuery(id+"F25.imprint","IMPRINT",FACE,{"disambiguationData":[TD([[makeQuery(id+"F25.imprint","IMPRINT",EDGE,{"derivedFrom":sQuery(id+"F25.wireOp",EDGE,"E83.bottom")}),1.0]])]});
            extrude(context, id + "F26", {"entities" : qUnion([Q0, Q1, Q2, Q3, Q4, Q5]), "depth" : 35 * mm});
        }
        {
            var Q0;
            Q0=makeQuery(id+"F26.opExtrude","SWEPT_FACE",FACE,{"disambiguationData":[OSD([sQuery(id+"F25.wireOp",EDGE,"E95.MirrorCS")])]});
            var sketch = newSketch(context, id + "F27", { "sketchPlane" : qUnion([Q0])});
            skLineSegment(sketch, "E102.bottom", {"start": v(-677.71, 0) * mm, "end": v(-328.76, 0) * mm});
            skLineSegment(sketch, "E102.top", {"start": v(-677.71, -25.48) * mm, "end": v(-328.76, -25.48) * mm});
            skLineSegment(sketch, "E102.left", {"start": v(-677.71, 0) * mm, "end": v(-677.71, -25.48) * mm});
            skLineSegment(sketch, "E102.right", {"start": v(-328.76, 0) * mm, "end": v(-328.76, -25.48) * mm});
            skSolve(sketch);
        }
        {
            var Q0;
            Q0=makeQuery(id+"F27.imprint","IMPRINT",FACE,{"disambiguationData":[TD([[makeQuery(id+"F27.imprint","IMPRINT",EDGE,{"derivedFrom":sQuery(id+"F27.wireOp",EDGE,"E102.bottom")}),-1.0]])]});
            var Q1;
            Q1=makeQuery(id+"F27.imprint","IMPRINT",FACE,{"disambiguationData":[TD([[makeQuery(id+"F27.imprint","IMPRINT",EDGE,{"derivedFrom":sQuery(id+"F27.wireOp",EDGE,"vdCn5M4T-uzS2-vMqU-omqx-BEMn8WxRvKta.bottom")}),-1.0]])]});
            extrude(context, id + "F28", {"entities" : qUnion([Q0, Q1]), "operationType" : NewBodyOperationType.REMOVE, "endBound" : BoundingType.THROUGH_ALL, "oppositeDirection" : true, "depth" : 25.4 * mm});
        }
        {
            var Q0;
            Q0=makeQuery(id+"F26.opExtrude","SWEPT_FACE",FACE,{"disambiguationData":[OSD([sQuery(id+"F25.wireOp",EDGE,"E100.MirrorCS")])]});
            var sketch = newSketch(context, id + "F29", { "sketchPlane" : qUnion([Q0])});
            skLineSegment(sketch, "E103.bottom", {"start": v(-677.71, 0) * mm, "end": v(-328.76, 0) * mm});
            skLineSegment(sketch, "E103.top", {"start": v(-677.71, -25.48) * mm, "end": v(-328.76, -25.48) * mm});
            skLineSegment(sketch, "E103.left", {"start": v(-677.71, 0) * mm, "end": v(-677.71, -25.48) * mm});
            skLineSegment(sketch, "E103.right", {"start": v(-328.76, 0) * mm, "end": v(-328.76, -25.48) * mm});
            skSolve(sketch);
        }
        {
            var Q0;
            Q0=makeQuery(id+"F29.imprint","IMPRINT",FACE,{"disambiguationData":[TD([[makeQuery(id+"F29.imprint","IMPRINT",EDGE,{"derivedFrom":sQuery(id+"F29.wireOp",EDGE,"E103.bottom")}),-1.0]])]});
            extrude(context, id + "F30", {"entities" : qUnion([Q0]), "operationType" : NewBodyOperationType.REMOVE, "oppositeDirection" : true, "depth" : 25.4 * mm});
        }
        {
            var Q0;
            Q0=makeQuery(id+"F26.opExtrude","SWEPT_FACE",FACE,{"disambiguationData":[OSD([sQuery(id+"F25.wireOp",EDGE,"E96.MirrorCS")])]});
            var sketch = newSketch(context, id + "F31", { "sketchPlane" : qUnion([Q0])});
            skLineSegment(sketch, "E104.bottom", {"start": v(-677.71, 0) * mm, "end": v(-328.76, 0) * mm});
            skLineSegment(sketch, "E104.top", {"start": v(-677.71, -25.48) * mm, "end": v(-328.76, -25.48) * mm});
            skLineSegment(sketch, "E104.left", {"start": v(-677.71, 0) * mm, "end": v(-677.71, -25.48) * mm});
            skLineSegment(sketch, "E104.right", {"start": v(-328.76, 0) * mm, "end": v(-328.76, -25.48) * mm});
            skSolve(sketch);
        }
        {
            var Q0;
            Q0=makeQuery(id+"F31.imprint","IMPRINT",FACE,{"disambiguationData":[TD([[makeQuery(id+"F31.imprint","IMPRINT",EDGE,{"derivedFrom":sQuery(id+"F31.wireOp",EDGE,"E104.bottom")}),-1.0]])]});
            extrude(context, id + "F32", {"entities" : qUnion([Q0]), "operationType" : NewBodyOperationType.REMOVE, "oppositeDirection" : true, "depth" : 25.4 * mm});
        }
        {
            var Q0;
            Q0=makeQuery(id+"F26.opExtrude","SWEPT_FACE",FACE,{"disambiguationData":[OSD([sQuery(id+"F25.wireOp",EDGE,"E81.top")])]});
            var sketch = newSketch(context, id + "F33", { "sketchPlane" : qUnion([Q0])});
            skLineSegment(sketch, "E105.bottom", {"start": v(328.76, 0) * mm, "end": v(677.71, 0) * mm});
            skLineSegment(sketch, "E105.top", {"start": v(328.76, -25.48) * mm, "end": v(677.71, -25.47) * mm});
            skLineSegment(sketch, "E105.left", {"start": v(328.76, 0) * mm, "end": v(328.76, -25.48) * mm});
            skLineSegment(sketch, "E105.right", {"start": v(677.71, 0) * mm, "end": v(677.71, -25.47) * mm});
            skSolve(sketch);
        }
        {
            var Q0;
            Q0=makeQuery(id+"F33.imprint","IMPRINT",FACE,{"disambiguationData":[TD([[makeQuery(id+"F33.imprint","IMPRINT",EDGE,{"derivedFrom":sQuery(id+"F33.wireOp",EDGE,"E105.bottom")}),1.0]])]});
            extrude(context, id + "F34", {"entities" : qUnion([Q0]), "operationType" : NewBodyOperationType.REMOVE, "oppositeDirection" : true, "depth" : 25.4 * mm});
        }
        {
            var Q0;
            Q0=makeQuery(id+"F26.opExtrude","SWEPT_FACE",FACE,{"disambiguationData":[OSD([sQuery(id+"F25.wireOp",EDGE,"E82.bottom")])]});
            var sketch = newSketch(context, id + "F35", { "sketchPlane" : qUnion([Q0])});
            skLineSegment(sketch, "E106.bottom", {"start": v(328.76, 0) * mm, "end": v(677.71, 0) * mm});
            skLineSegment(sketch, "E106.top", {"start": v(328.76, -25.48) * mm, "end": v(677.71, -25.48) * mm});
            skLineSegment(sketch, "E106.left", {"start": v(328.76, 0) * mm, "end": v(328.76, -25.48) * mm});
            skLineSegment(sketch, "E106.right", {"start": v(677.71, 0) * mm, "end": v(677.71, -25.47) * mm});
            skSolve(sketch);
        }
        {
            var Q0;
            Q0=makeQuery(id+"F35.imprint","IMPRINT",FACE,{"disambiguationData":[TD([[makeQuery(id+"F35.imprint","IMPRINT",EDGE,{"derivedFrom":sQuery(id+"F35.wireOp",EDGE,"E106.bottom")}),1.0]])]});
            extrude(context, id + "F36", {"entities" : qUnion([Q0]), "operationType" : NewBodyOperationType.REMOVE, "oppositeDirection" : true, "depth" : 25.4 * mm});
        }
        {
            var Q0;
            Q0=makeQuery(id+"F26.opExtrude","SWEPT_FACE",FACE,{"disambiguationData":[OSD([sQuery(id+"F25.wireOp",EDGE,"E83.bottom")])]});
            var sketch = newSketch(context, id + "F37", { "sketchPlane" : qUnion([Q0])});
            skLineSegment(sketch, "E107.bottom", {"start": v(328.76, 0) * mm, "end": v(677.71, 0) * mm});
            skLineSegment(sketch, "E107.top", {"start": v(328.76, -25.48) * mm, "end": v(677.71, -25.48) * mm});
            skLineSegment(sketch, "E107.left", {"start": v(328.76, 0) * mm, "end": v(328.76, -25.48) * mm});
            skLineSegment(sketch, "E107.right", {"start": v(677.71, 0) * mm, "end": v(677.71, -25.47) * mm});
            skSolve(sketch);
        }
        {
            var Q0;
            Q0=makeQuery(id+"F37.imprint","IMPRINT",FACE,{"disambiguationData":[TD([[makeQuery(id+"F37.imprint","IMPRINT",EDGE,{"derivedFrom":sQuery(id+"F37.wireOp",EDGE,"E107.bottom")}),1.0]])]});
            extrude(context, id + "F38", {"entities" : qUnion([Q0]), "operationType" : NewBodyOperationType.REMOVE, "oppositeDirection" : true, "depth" : 25.4 * mm});
        }
        {
            var Q0;
            Q0=makeQuery(id+"F20.opExtrude","CAP_FACE",FACE,{"disambiguationData":[OSD([sQuery(id+"F19.wireOp",EDGE,"E77.bottom"),sQuery(id+"F19.wireOp",EDGE,"E77.top"),sQuery(id+"F19.wireOp",EDGE,"E77.left"),sQuery(id+"F19.wireOp",EDGE,"E77.right")])],"isStart":false});
            var sketch = newSketch(context, id + "F39", { "sketchPlane" : qUnion([Q0])});
            skLineSegment(sketch, "E108.bottom", {"start": v(262.73, 74.61) * mm, "end": v(-262.73, 74.61) * mm});
            skLineSegment(sketch, "E108.top", {"start": v(262.73, 458.79) * mm, "end": v(-262.73, 458.79) * mm});
            skLineSegment(sketch, "E108.left", {"start": v(262.73, 74.61) * mm, "end": v(262.73, 458.79) * mm});
            skLineSegment(sketch, "E108.right", {"start": v(-262.73, 74.61) * mm, "end": v(-262.73, 458.79) * mm});
            skPoint(sketch, "E108.middle", {"position": v(0, 266.7) * mm});
            skPoint(sketch, "E108.middle.positionSnap0", {"position": v(-762, 266.7) * mm});
            skPoint(sketch, "E108.middle.positionSnap1", {"position": v(0, 533.4) * mm});
            skPoint(sketch, "E108.centerSnap0", {"position": v(-762, 266.7) * mm});
            skPoint(sketch, "E108.centerSnap1", {"position": v(0, 533.4) * mm});
            skSolve(sketch);
        }
        {
            var Q0;
            Q0=makeQuery(id+"F39.imprint","IMPRINT",FACE,{"disambiguationData":[TD([[makeQuery(id+"F39.imprint","IMPRINT",EDGE,{"derivedFrom":sQuery(id+"F39.wireOp",EDGE,"E108.bottom")}),-1.0]])]});
            extrude(context, id + "F40", {"entities" : qUnion([Q0]), "depth" : 50.8 * mm});
        }
        {
            var Q0;
            Q0=makeQuery(id+"F40.opExtrude","SWEPT_EDGE",EDGE,{"disambiguationData":[OSD([sQuery(id+"F39.wireOp",EDGE,"E108.bottom"),sQuery(id+"F39.wireOp",EDGE,"E108.right")])]});
            var Q1;
            Q1=makeQuery(id+"F40.opExtrude","SWEPT_EDGE",EDGE,{"disambiguationData":[OSD([sQuery(id+"F39.wireOp",EDGE,"E108.bottom"),sQuery(id+"F39.wireOp",EDGE,"E108.left")])]});
            var Q2;
            Q2=makeQuery(id+"F40.opExtrude","SWEPT_EDGE",EDGE,{"disambiguationData":[OSD([sQuery(id+"F39.wireOp",EDGE,"E108.top"),sQuery(id+"F39.wireOp",EDGE,"E108.right")])]});
            var Q3;
            Q3=makeQuery(id+"F40.opExtrude","SWEPT_EDGE",EDGE,{"disambiguationData":[OSD([sQuery(id+"F39.wireOp",EDGE,"E108.top"),sQuery(id+"F39.wireOp",EDGE,"E108.left")])]});
            fillet(context, id + "F41", {"entities" : qUnion([Q0, Q1, Q2, Q3]), "radius" : (4 + (9 / 16)) * mm, "tangentPropagation" : true, "allowEdgeOverflow" : false});
        }
        {
            var Q0;
            Q0=makeQuery(id+"F40.opExtrude","CAP_FACE",FACE,{"disambiguationData":[OSD([sQuery(id+"F39.wireOp",EDGE,"E108.bottom"),sQuery(id+"F39.wireOp",EDGE,"E108.top"),sQuery(id+"F39.wireOp",EDGE,"E108.left"),sQuery(id+"F39.wireOp",EDGE,"E108.right")])],"isStart":false});
            shell(context, id + "F42", {"entities" : qUnion([Q0]), "thickness" : 12.7 * mm});
        }
        {
            var Q0;
            Q0=makeQuery(id+"F40.opExtrude","CAP_FACE",FACE,{"disambiguationData":[OSD([sQuery(id+"F39.wireOp",EDGE,"E108.bottom"),sQuery(id+"F39.wireOp",EDGE,"E108.top"),sQuery(id+"F39.wireOp",EDGE,"E108.left"),sQuery(id+"F39.wireOp",EDGE,"E108.right")])],"isStart":false});
            fillet(context, id + "F43", {"entities" : qUnion([Q0]), "radius" : 5.08 * mm, "tangentPropagation" : true, "allowEdgeOverflow" : false});
        }
        {
            var Q0;
            Q0=makeQuery(id+"F42.opShell","OFFSET_FACE",FACE,{"disambiguationData":[OSD([sQuery(id+"F39.wireOp",EDGE,"E108.bottom"),sQuery(id+"F39.wireOp",EDGE,"E108.top"),sQuery(id+"F39.wireOp",EDGE,"E108.left"),sQuery(id+"F39.wireOp",EDGE,"E108.right")])]});
            fillet(context, id + "F44", {"entities" : qUnion([Q0]), "radius" : 152.4 * mm, "tangentPropagation" : true, "allowEdgeOverflow" : false});
        }
        {
            var Q0;
            Q0=makeQuery(id+"F42.opShell","OFFSET_FACE",FACE,{"disambiguationData":[OSD([sQuery(id+"F39.wireOp",EDGE,"E108.bottom"),sQuery(id+"F39.wireOp",EDGE,"E108.top"),sQuery(id+"F39.wireOp",EDGE,"E108.left"),sQuery(id+"F39.wireOp",EDGE,"E108.right")])]});
            var sketch = newSketch(context, id + "F45", { "sketchPlane" : qUnion([Q0])});
            skPoint(sketch, "E109", {"position": v(0, 266.7) * mm});
            skPoint(sketch, "E109.positionSnap0", {"position": v(-152.4, 266.7) * mm});
            skPoint(sketch, "E109.positionSnap1", {"position": v(0, 348.46) * mm});
            skSolve(sketch);
        }
        {
            var Q0;
            Q0=sQuery(id+"F45.wireOp",VERTEX,"E109");
            var Q1;
            Q1=makeQuery(id+"F40.opExtrude","SWEPT_BODY",BODY,{"disambiguationData":[OSD([sQuery(id+"F39.wireOp",EDGE,"E108.bottom"),sQuery(id+"F39.wireOp",EDGE,"E108.top"),sQuery(id+"F39.wireOp",EDGE,"E108.left"),sQuery(id+"F39.wireOp",EDGE,"E108.right")])]});
            hole(context, id + "F46", {"style" : HoleStyle.C_SINK, "endStyle" : HoleEndStyle.BLIND, "holeDiameter" : 50.8 * mm, "cSinkDiameter" : 63.5 * mm, "cSinkAngle" : 82 * degree, "holeDepth" : 25.4 * mm, "isTappedThrough" : true, "tappedDepth" : 12.7 * mm, "tapClearance" : 3, "locations" : qUnion([Q0]), "scope" : qUnion([Q1])});
        }
    });
